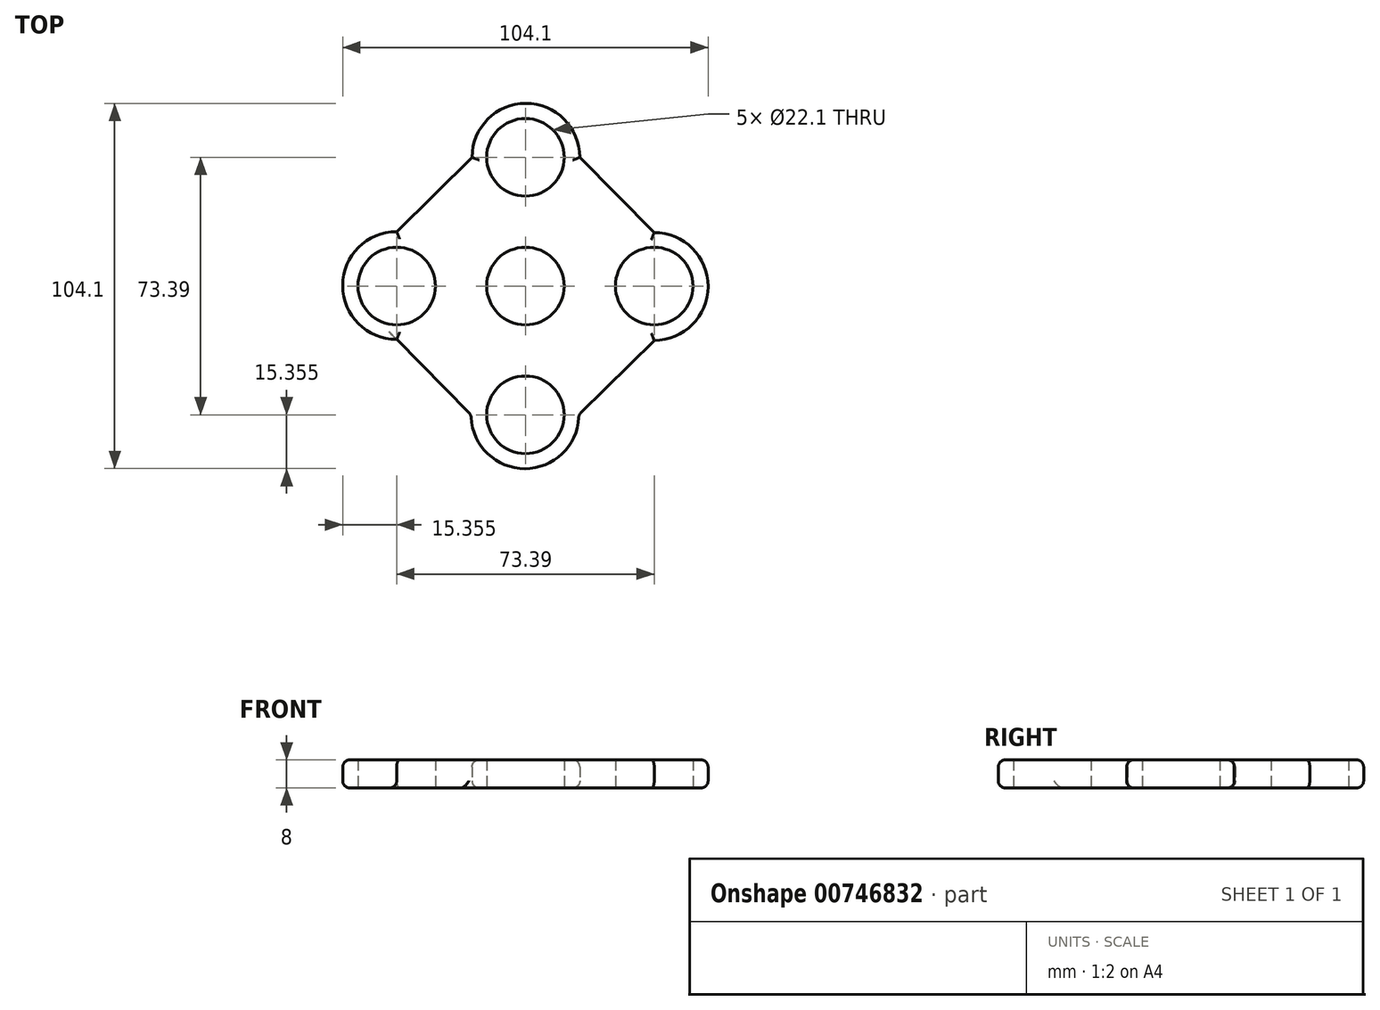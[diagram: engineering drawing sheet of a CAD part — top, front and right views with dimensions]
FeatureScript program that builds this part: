
annotation { "Feature Type Name" : "Feature", "Feature Type Description" : "" }
export const myFeature = defineFeature(function(context is Context, id is Id, definition is map)
    precondition{}
    {
        {
            var Q0;
            Q0=qCreatedBy(makeId("Top.planeOp"),FACE);
            var sketch = newSketch(context, id + "F0", { "sketchPlane" : qUnion([Q0])});
            skCircle(sketch, "E0", {"center": v(0, 0) * mm, "radius": 11.05 * mm});
            skCircle(sketch, "E1", {"center": v(0, 36.7) * mm, "radius": 11.05 * mm});
            skCircle(sketch, "E2.1.0", {"center": v(-36.7, 0) * mm, "radius": 11.05 * mm});
            skCircle(sketch, "E3.1.2.0", {"center": v(0, -36.7) * mm, "radius": 11.05 * mm});
            skCircle(sketch, "E3.1.3.0", {"center": v(36.7, 0) * mm, "radius": 11.05 * mm});
            skArc(sketch, "E4", {"start": v(15.5, 36.7) * mm, "mid": v(0.14, 52.05) * mm, "end": v(-15.21, 36.7) * mm});
            skArc(sketch, "E5.1.0", {"start": v(-36.7, 15.5) * mm, "mid": v(-52.05, 0.14) * mm, "end": v(-36.7, -15.21) * mm});
            skArc(sketch, "E5.2.0", {"start": v(-15.5, -36.7) * mm, "mid": v(-0.14, -52.05) * mm, "end": v(15.21, -36.7) * mm});
            skArc(sketch, "E5.3.0", {"start": v(36.7, -15.5) * mm, "mid": v(52.05, -0.14) * mm, "end": v(36.7, 15.21) * mm});
            skLineSegment(sketch, "E6", {"start": v(-36.7, 15.5) * mm, "end": v(-15.21, 36.7) * mm});
            skLineSegment(sketch, "E7", {"start": v(15.5, 36.7) * mm, "end": v(36.7, 15.21) * mm});
            skLineSegment(sketch, "E8", {"start": v(36.7, -15.5) * mm, "end": v(15.21, -36.7) * mm});
            skLineSegment(sketch, "E9", {"start": v(-15.5, -36.7) * mm, "end": v(-36.7, -15.21) * mm});
            skSolve(sketch);
        }
        {
            var Q0;
            Q0 = qSketchRegion(id + "F0", true);
            extrude(context, id + "F1", {"entities" : qUnion([Q0]), "depth" : 8 * mm, "offsetDistance" : 25.4 * mm});
        }
        {
            var Q0;
            Q0=makeQuery(id+"F1.opExtrude","CAP_EDGE",EDGE,{"disambiguationData":[OSD([sQuery(id+"F0.wireOp",EDGE,"E6")])],"isStart":false});
            var Q1;
            Q1=makeQuery(id+"F1.opExtrude","CAP_EDGE",EDGE,{"disambiguationData":[OSD([sQuery(id+"F0.wireOp",EDGE,"E4")])],"isStart":false});
            var Q2;
            Q2=makeQuery(id+"F1.opExtrude","CAP_EDGE",EDGE,{"disambiguationData":[OSD([sQuery(id+"F0.wireOp",EDGE,"E7")])],"isStart":false});
            var Q3;
            Q3=makeQuery(id+"F1.opExtrude","CAP_EDGE",EDGE,{"disambiguationData":[OSD([sQuery(id+"F0.wireOp",EDGE,"E5.3.0")])],"isStart":false});
            var Q4;
            Q4=makeQuery(id+"F1.opExtrude","CAP_EDGE",EDGE,{"disambiguationData":[OSD([sQuery(id+"F0.wireOp",EDGE,"E8")])],"isStart":false});
            var Q5;
            Q5=makeQuery(id+"F1.opExtrude","CAP_EDGE",EDGE,{"disambiguationData":[OSD([sQuery(id+"F0.wireOp",EDGE,"E5.2.0")])],"isStart":false});
            var Q6;
            Q6=makeQuery(id+"F1.opExtrude","CAP_EDGE",EDGE,{"disambiguationData":[OSD([sQuery(id+"F0.wireOp",EDGE,"E9")])],"isStart":false});
            var Q7;
            Q7=makeQuery(id+"F1.opExtrude","CAP_EDGE",EDGE,{"disambiguationData":[OSD([sQuery(id+"F0.wireOp",EDGE,"E5.1.0")])],"isStart":false});
            var Q8;
            Q8=makeQuery(id+"F1.opExtrude","SWEPT_FACE",FACE,{"disambiguationData":[OSD([sQuery(id+"F0.wireOp",EDGE,"E5.2.0")])]});
            var Q9;
            Q9=makeQuery(id+"F1.opExtrude","CAP_EDGE",EDGE,{"disambiguationData":[OSD([sQuery(id+"F0.wireOp",EDGE,"E8")])],"isStart":true});
            var Q10;
            Q10=makeQuery(id+"F1.opExtrude","CAP_EDGE",EDGE,{"disambiguationData":[OSD([sQuery(id+"F0.wireOp",EDGE,"E5.3.0")])],"isStart":true});
            var Q11;
            Q11=makeQuery(id+"F1.opExtrude","CAP_EDGE",EDGE,{"disambiguationData":[OSD([sQuery(id+"F0.wireOp",EDGE,"E7")])],"isStart":true});
            var Q12;
            Q12=makeQuery(id+"F1.opExtrude","CAP_EDGE",EDGE,{"disambiguationData":[OSD([sQuery(id+"F0.wireOp",EDGE,"E4")])],"isStart":true});
            var Q13;
            Q13=makeQuery(id+"F1.opExtrude","CAP_EDGE",EDGE,{"disambiguationData":[OSD([sQuery(id+"F0.wireOp",EDGE,"E6")])],"isStart":true});
            var Q14;
            Q14=makeQuery(id+"F1.opExtrude","CAP_EDGE",EDGE,{"disambiguationData":[OSD([sQuery(id+"F0.wireOp",EDGE,"E5.1.0")])],"isStart":true});
            fillet(context, id + "F2", {"entities" : qUnion([Q0, Q1, Q2, Q3, Q4, Q5, Q6, Q7, Q8, Q9, Q10, Q11, Q12, Q13, Q14]), "radius" : 2 * mm, "tangentPropagation" : true, "allowEdgeOverflow" : false});
        }
    });
